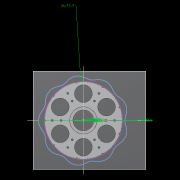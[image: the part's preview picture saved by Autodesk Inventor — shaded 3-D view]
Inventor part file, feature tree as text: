
AUTODESK INVENTOR PART (.ipt)
format: ipt  version: 2022.2 (Build 262287010, 287A)  size: 624,640 bytes
history: native  units: mm
features: other x19, extrude x15, sketch x9, pattern_circular x7, fillet x2, move_body x2, revolve x2, draft x2, plane x2, chamfer x2
ambient origin geometry x8: Origin, YZ Plane, XZ Plane, XY Plane, X Axis, Y Axis, Z Axis, Center Point
bodies: Solid5 (feature_tree)
feature tree (62):
  other  "CrossSection1"
  sketch  "Sketch7"  dims[d90=15.767323mm]
  other  "Roller1"
  other  "Roller2"
  sketch  "Sketch22"  dims[d167=8.972256mm]
  sketch  "Sketch2"  dims[d57=4.025mm]
  sketch  "Sketch23"  dims[d173=10.814812mm]
  other  "RevRoller1"
  fillet  "Fillet1"  Radius=13.336791mm
  pattern_circular  "Circular Pattern13"  Count=360  [1 undecoded]
  move_body  "Move Body7"
  revolve  "Revolution13"  [1 undecoded]
  fillet  "Fillet3"  Radius=0.025mm
  pattern_circular  "Circular Pattern14"  [2 undecoded]
  move_body  "Move Body6"
  revolve  "Revolution14"  [1 undecoded]
  other  "OuterRim_Top2"
  other  "OuterRim_Bottom2"
  extrude  "Rotor_Ring"  Depth=3.0mm
  draft  "FaceDraft2"
  sketch  "Sketch30"  dims[d201=53.5mm d232=0.0mm d233=3600.0mm]
  plane  "Work Plane5"
  other  "Rotor Featurs"
  other  "RotorRim_Bottom"
  extrude  "Extrusion24"  Depth=3.0mm
  extrude  "Extrusion25"  Depth=0.1mm
  extrude  "Extrusion26"  Depth=3.0mm
  pattern_circular  "Circular Pattern23"  [2 undecoded]
  sketch  "Sketch41"  dims[d346=0.025mm]
  extrude  "Extrusion27"  Depth=3.0mm
  extrude  "Extrusion28"  TaperAngle=90.0deg  [1 undecoded]
  pattern_circular  "Circular Pattern24"  [2 undecoded]
  extrude  "Extrusion29"  Depth=3.0mm
  extrude  "Extrusion30"  TaperAngle=360.0deg  [1 undecoded]
  extrude  "Extrusion31"  TaperAngle=30.0deg  [1 undecoded]
  pattern_circular  "Circular Pattern25"  [2 undecoded]
  sketch  "Sketch42"  dims[d347=0.1mm]
  extrude  "Extrusion32"  Depth=3.0mm
  extrude  "Extrusion33"  Depth=0.1mm
  extrude  "Extrusion34"  Depth=3.0mm
  extrude  "Extrusion35"  TaperAngle=30.0deg  [1 undecoded]
  pattern_circular  "Circular Pattern26"  Angle=90.0deg  [1 undecoded]
  pattern_circular  "Circular Pattern27"  [2 undecoded]
  chamfer  "Chamfer1"  Distance=60.0mm
  chamfer  "Chamfer2"  Angle=360.0deg  [1 undecoded]
  draft  "FaceDraft4"
  plane  "Work Plane6"
  sketch  "Sketch43"  dims[d348=0.1mm d349=17.374602mm d350=17.374329mm d351=0.025mm d352=0.025mm d354=0.1mm d355=17.374329mm d356=17.374602mm d357=1.0mm d358=90.0deg d359=0.5mm d360=60.0mm d361=360.0deg d363=30.0deg d367=8.1mm d369=4.014775mm d370=0.1mm d371=1.0mm d372=30.0deg d373=90.0deg d374=0.5mm d375=60.0mm d376=360.0deg d378=90.0deg d379=0.1mm d380=0.1mm d381=0.1mm d382=0.1mm d383=0.1mm d384=10.461905mm d385=0.0mm d386=0.0mm d391=1.0mm d392=53.5mm d393=1.5mm d394=1.5mm d395=1.5mm d396=1.5mm d397=90.0deg d398=90.0deg d399=90.0deg d400=53.5mm d401=10.461905mm d402=0.0mm d486=0.436332mm d487=0.5mm d488=2.0mm d489=0.0mm d490=20.0mm d495=2.5mm d496=8.0mm d506=13.856406mm d507=55.5mm d508=8.0mm d509=0.05mm d510=2.5mm d511=30.0deg d512=12.0mm d513=6.0mm d514=0.2mm d515=30.0deg d516=131.0mm d517=65.5mm d518=0.2mm d519=100.0mm d520=120.0mm d521=2.0mm d522=150.0mm d530=50.0mm d531=5.5mm d532=5.5mm d533=5.5mm d534=85.75mm d535=73.5mm d536=61.25mm d537=24.5mm d538=3.0mm d539=2.4mm d540=0.0mm d541=0.0mm d542=0.0mm d543=5.5mm d544=3.0mm d545=0.0mm d546=90.0mm d547=360.0deg d549=3.0mm d550=3.0mm d551=2.4mm d552=0.0mm d553=5.230953mm d554=0.0mm d555=2.4mm d556=0.0mm d557=5.230953mm d558=0.0mm d559=5.230953mm d560=0.0mm d561=90.0mm d562=360.0deg d564=60.0mm d565=360.0deg d567=5.5mm d568=5.5mm d569=3.0mm d570=0.0mm d571=5.230953mm d572=0.0mm d573=3.0mm d574=0.0mm d575=5.230953mm d576=0.0mm d577=90.0mm d578=360.0deg d580=60.0mm d581=360.0deg d584=20.0mm d585=8.0mm d587=1.75mm d589=3.0mm d592=2.0mm d593=12.0mm d594=12.0mm d600=0.5mm d601=2.0mm d602=45.0deg d603=0.5mm d604=2.0mm d605=45.0deg d606=0.436332mm d607=0.5mm d608=0.0mm d609=20.0mm d611=360.0deg d613=0.0mm d614=0.0mm d16=0.872665mm d17=0.872665mm d49=0.872665mm d50=0.872665mm d51=0.872665mm d52=0.872665mm d236=0.5mm d237=0.872665mm d238=0.5mm d239=0.872665mm d282=1.0mm d283=1.0mm d284=1.0mm d285=0.15mm d286=0.25mm d287=0.375mm d288=14.3117mm d289=0.75mm d290=20.594885mm d291=0.0625mm d292=0.75mm d293=0.375mm d405=0.5mm d406=0.872665mm d407=0.5mm d408=0.872665mm d413=0.5mm d414=0.872665mm d415=0.5mm d416=0.872665mm d417=0.5mm d418=0.872665mm d419=0.5mm d420=0.872665mm d421=0.872665mm d431=0.5mm d432=0.872665mm d433=0.5mm d434=0.872665mm d471=0.5mm d472=0.872665mm d473=0.5mm d474=0.872665mm d497=0.5mm d498=0.872665mm d499=0.5mm d500=0.872665mm d590=0.5mm d591=0.872665mm]
  extrude  "Extrusion37"  TaperAngle=90.0deg  [1 undecoded]
  extrude  "Extrusion38"  Depth=0.1mm
  other  "2D Equation Curve1"
  sketch  "Sketch40"  dims[d343=17.374329mm d344=17.374602mm d345=0.025mm]
  other  "Work Axis6"
  other  "Work Axis7"
  other  "Work Axis8"
  other  "Work Axis9"
  other  "Work Axis10"
  other  "Work Point1"
  other  "Work Point2"
  other  "Work Point3"
  other  "Work Point4"
  other  "Work Point5"
note: 20 required parameter values undecoded (feature->parameter linkage not recoverable at this tier; creation-order binding heuristic only, values carry confidence <= 0.55)